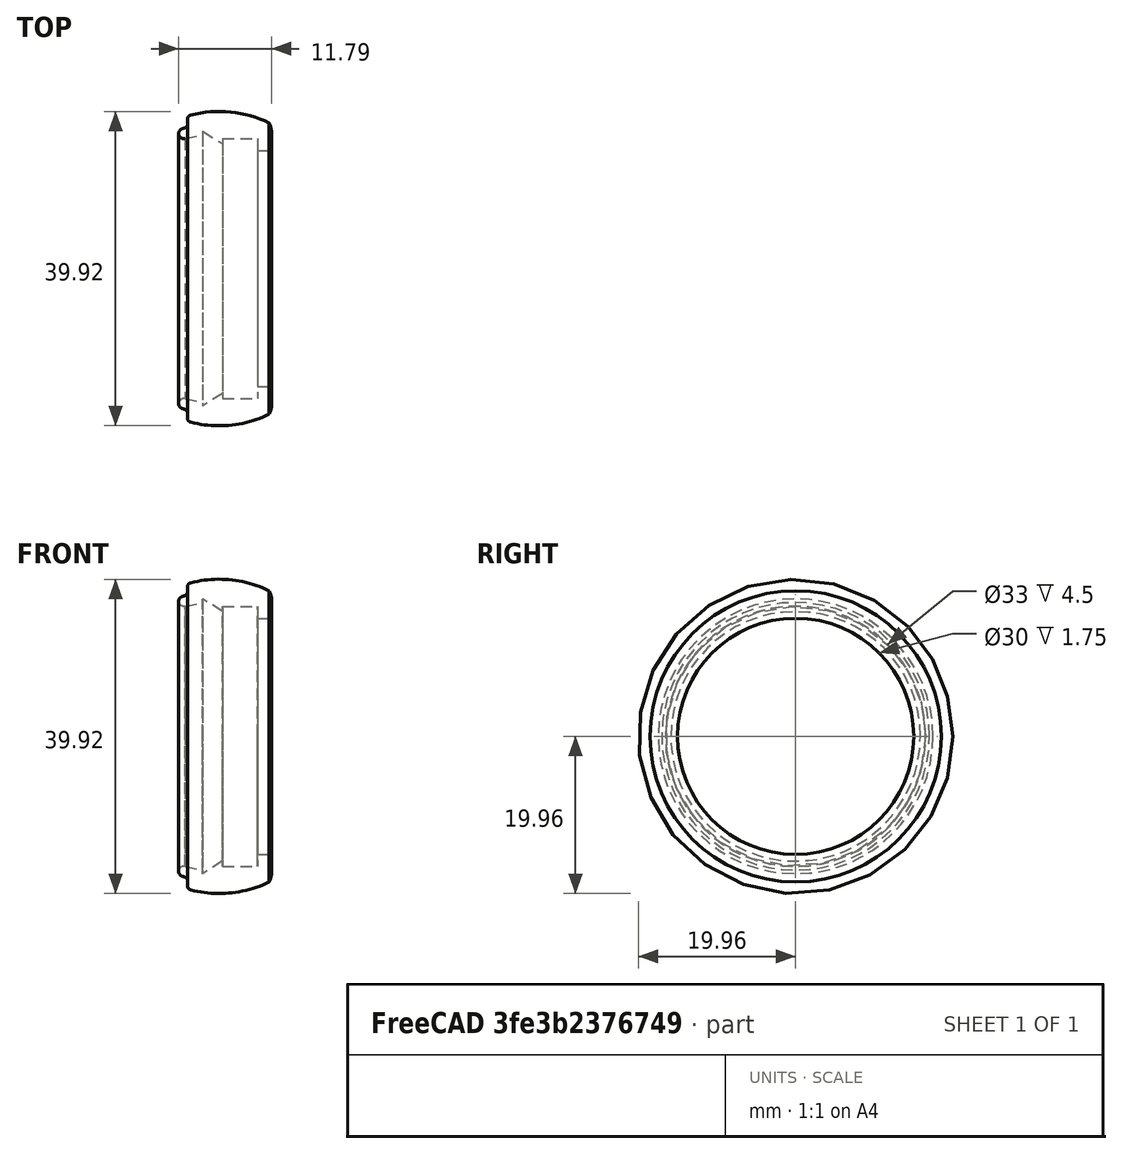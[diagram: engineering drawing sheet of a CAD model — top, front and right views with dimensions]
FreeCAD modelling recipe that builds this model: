
FCSTD DOCUMENT  (FreeCAD 0.15R4671 (Git))
Label: TestCase
License: All rights reserved
LicenseURL: http://en.wikipedia.org/wiki/All_rights_reserved
objects: Sketcher::SketchObject×1, PartDesign::Revolution×1
note: 3 computed .brp shape members not serialized (recipe doc carries the construction recipe); baked Part::Feature solids carry a one-line shape summary decoded from their .brp

FEATURE [Sketcher::SketchObject] Sketch
  sketch-geometry (13):
    g0: ArcOfCircle CenterX=1.98578 CenterY=5.413 CenterZ=0 NormalX=0 NormalY=0 NormalZ=1 Radius=14.55 StartAngle=1.11851 EndAngle=1.82375
    g1: ArcOfCircle CenterX=-1.53039 CenterY=19.0159 CenterZ=0 NormalX=0 NormalY=0 NormalZ=1 Radius=0.5 StartAngle=1.82375 EndAngle=3.47698
    g2: ArcOfCircle CenterX=-2.75796 CenterY=18.588 CenterZ=0 NormalX=0 NormalY=0 NormalZ=1 Radius=0.8 StartAngle=4.88551 EndAngle=6.61857
    g3: ArcOfCircle CenterX=-2.50818 CenterY=17.1597 CenterZ=0 NormalX=0 NormalY=0 NormalZ=1 Radius=0.65 StartAngle=1.74393 EndAngle=4.9339
    g4: LineSegment StartX=-2.36537 StartY=16.5256 StartZ=0 EndX=-0.115366 EndY=17 EndZ=0
    g5: ArcOfCircle CenterX=6.00813 CenterY=17.3 CenterZ=0 NormalX=0 NormalY=0 NormalZ=1 Radius=2.6265 StartAngle=6.28319 EndAngle=6.75767
    g6: LineSegment StartX=-0.115366 StartY=17 StartZ=0 EndX=-0.115366 EndY=17.4509 EndZ=0
    g7: LineSegment StartX=-0.115366 StartY=17.4509 StartZ=0 EndX=2.38463 EndY=15.8509 EndZ=0
    g8: LineSegment StartX=2.38463 StartY=15.8509 StartZ=0 EndX=2.38463 EndY=16.5 EndZ=0
    g9: LineSegment StartX=2.38463 StartY=16.5 StartZ=0 EndX=6.88463 EndY=16.5 EndZ=0
    g10: LineSegment StartX=6.88463 StartY=16.5 StartZ=0 EndX=6.88463 EndY=15 EndZ=0
    g11: LineSegment StartX=6.88463 StartY=15 StartZ=0 EndX=8.63463 EndY=15 EndZ=0
    g12: LineSegment StartX=8.63463 StartY=15 StartZ=0 EndX=8.63463 EndY=17.3 EndZ=0
  constraints (44):
    c: Coincident(g4,g3)
    c: Coincident(g0,g1)
    c: Coincident(g1,g2)
    c: Coincident(g2,g3)
    c: Tangent(g1,g2)
    c: Tangent(g2,g3)
    c: Tangent(g1,g0)
    c: Coincident(g6,g4)
    c: Vertical(g6)
    c: Coincident(g6,g7)
    c: Coincident(g7,g8)
    c: Coincident(g8,g9)
    c: Horizontal(g9)
    c: Coincident(g9,g10)
    c: Coincident(g10,g11)
    c: Horizontal(g11)
    c: Coincident(g11,g12)
    c: Vertical(g12)
    c: Vertical(g10)
    c: Coincident(g5,g12)
    c: Tangent(g5,g12)
    c: Coincident(g0,g5)
    c: DistanceY(g3) = 16.5256
    c: DistanceY(g4) = 17
    c: DistanceX(g3,g4) = 2.25
    c: DistanceY(g4,g6) = 0.450876
    c: DistanceX(g6,g8) = 2.5
    c: Vertical(g8)
    c: DistanceY(g7,g6) = 1.6
    c: DistanceX(g8,g9) = 4.5
    c: DistanceX(g11,g10) = -1.75
    c: DistanceY(g0,g11) = -3.5
    c: DistanceY(g9,g10) = -1.5
    c: DistanceX(g0,g0) = 10
    c: Radius(g1) = 0.5
    c: Radius(g2) = 0.8
    c: Radius(g3) = 0.65
    c: Radius(g5) = 2.6265
    c: Radius(g0) = 14.55
    c: DistanceY(g0) = 19.5
    c: DistanceY(g0) = 18.5
    c: DistanceY(g5) = 17.3
    c: DistanceX(g9) = 6.88463
    c: DistanceY(g2) = 17.8
FEATURE [PartDesign::Revolution] Revolution
  Angle = 360
  Axis = (1,0,0)
  Base = (0,0,0)
  ReferenceAxis = -> Sketch [H_Axis]
  Sketch = -> Sketch
